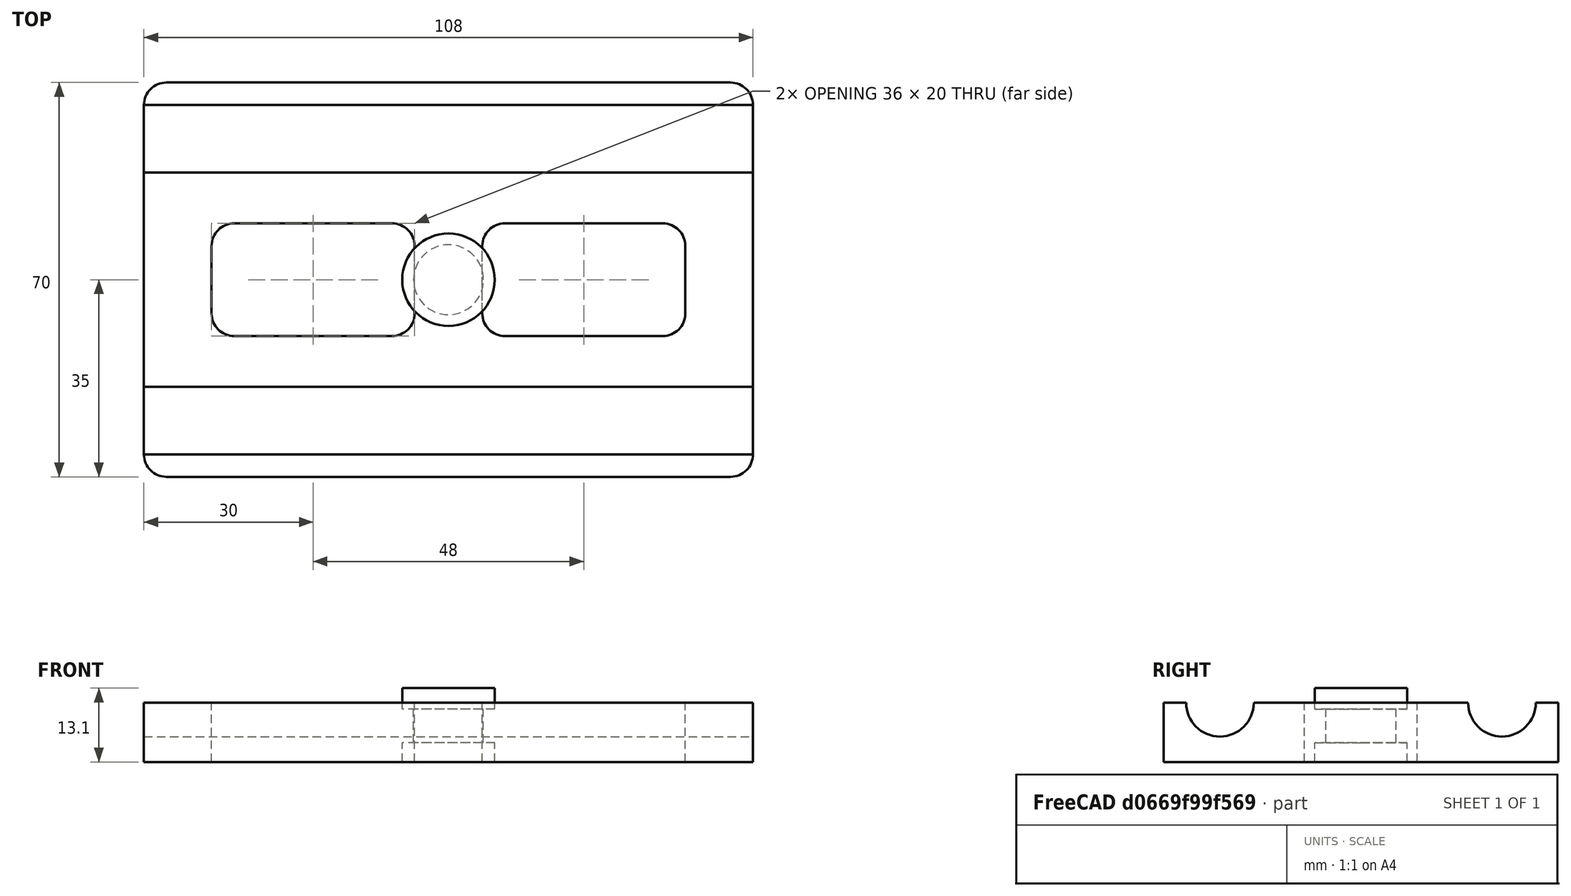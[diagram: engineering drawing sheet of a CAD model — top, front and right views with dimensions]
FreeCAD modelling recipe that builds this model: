
FCSTD DOCUMENT  (FreeCAD 0.15R4671 (Git))
Label: carriage_bolt
License: All rights reserved
LicenseURL: http://en.wikipedia.org/wiki/All_rights_reserved
objects: Part::Cylinder×5, Part::Box×3, Part::Fillet×3, Part::MultiFuse×1, Part::Cut×1
note: 13 computed .brp shape members not serialized (recipe doc carries the construction recipe); baked Part::Feature solids carry a one-line shape summary decoded from their .brp

FEATURE [Part::Cylinder] extr_outup
  Angle = 360
  Height = 3.7
  Placement = pos=(0,0,9.4) rot=(0,0,1;0rad)
  Radius = 8.2
FEATURE [Part::Cylinder] extr_in
  Angle = 360
  Height = 6
  Placement = pos=(0,0,3.4) rot=(0,0,1;0rad)
  Radius = 6.2
FEATURE [Part::Cylinder] extr_outbot
  Angle = 360
  Height = 3.4
  Radius = 8.2
FEATURE [Part::Box] total_box
  Height = 10.5
  Length = 108
  Placement = pos=(-54,-35,0) rot=(0,0,1;0rad)
  Width = 70
FEATURE [Part::Fillet] tot_box_fllt
  Base = -> total_box
  Edges = 4 edges r=4: [Edge1,Edge3,Edge5,Edge7]
FEATURE [Part::Box] inrect_p
  Height = 12.5
  Length = 36
  Placement = pos=(6,-10,-1) rot=(0,0,1;0rad)
  Width = 20
FEATURE [Part::Box] inrect_n
  Height = 12.5
  Length = 36
  Placement = pos=(-42,-10,-1) rot=(0,0,1;0rad)
  Width = 20
FEATURE [Part::Fillet] inrect_p_fllt
  Base = -> inrect_p
  Edges = 4 edges r=4: [Edge1,Edge3,Edge5,Edge7]
FEATURE [Part::Fillet] inrect_n_fllt
  Base = -> inrect_n
  Edges = 4 edges r=4: [Edge1,Edge3,Edge5,Edge7]
FEATURE [Part::Cylinder] rod_p
  Angle = 360
  Height = 110
  Placement = pos=(-55,25,10.5) rot=(0,1,0;1.5708rad)
  Radius = 6
FEATURE [Part::Cylinder] rod_n
  Angle = 360
  Height = 110
  Placement = pos=(-55,-25,10.5) rot=(0,1,0;1.5708rad)
  Radius = 6
FEATURE [Part::MultiFuse] fuse_holes
  Shapes = -> [inrect_p_fllt,inrect_n_fllt,rod_n,rod_p]
FEATURE [Part::Cut] carr_hole
  Base = -> tot_box_fllt
  Tool = -> fuse_holes
